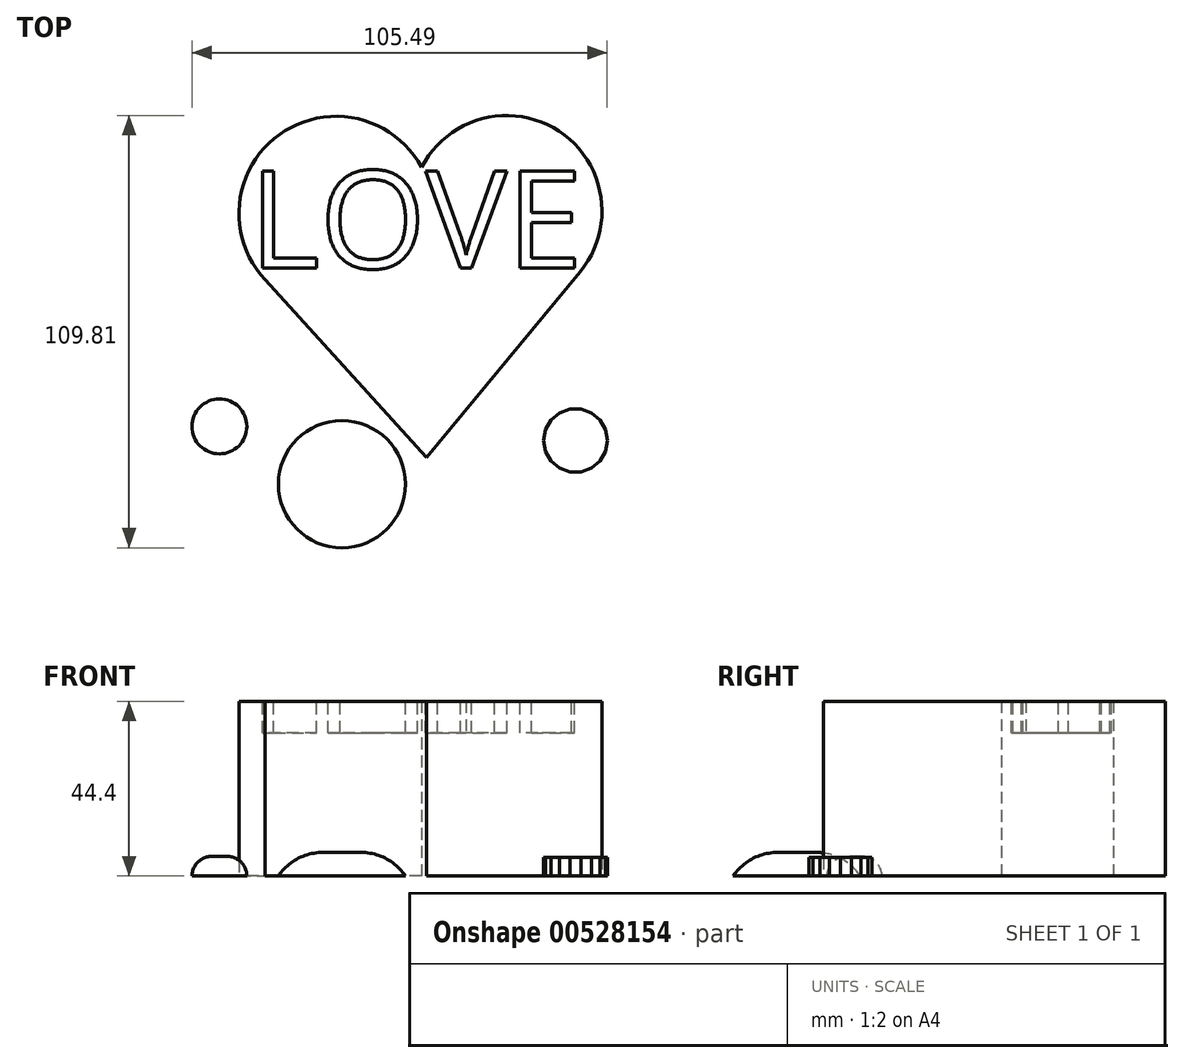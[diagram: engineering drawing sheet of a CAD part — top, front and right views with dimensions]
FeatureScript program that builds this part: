
annotation { "Feature Type Name" : "Feature", "Feature Type Description" : "" }
export const myFeature = defineFeature(function(context is Context, id is Id, definition is map)
    precondition{}
    {
        {
            var Q0;
            Q0=qCreatedBy(makeId("Top.planeOp"),FACE);
            var sketch = newSketch(context, id + "F0", { "sketchPlane" : qUnion([Q0])});
            skCircle(sketch, "E0", {"center": v(17.8, 25.02) * mm, "radius": 24.26 * mm});
            skCircle(sketch, "E1", {"center": v(-25.48, 24.4) * mm, "radius": 24.67 * mm});
            skLineSegment(sketch, "E2", {"start": v(-43.5, 7.56) * mm, "end": v(-2.46, -37.6) * mm});
            skLineSegment(sketch, "E3", {"start": v(-2.46, -37.6) * mm, "end": v(36.51, 9.57) * mm});
            skSolve(sketch);
        }
        {
            var Q0;
            {var subQ0=sQuery(id+"F0.wireOp",EDGE,"E1");var subQ1=sQuery(id+"F0.wireOp",EDGE,"E0");var subQ2=makeQuery(id+"F0.imprint","INTERSECT",VERTEX,{"disambiguationData":[OD(0.0)],"derivedFrom":[subQ1,subQ0]});Q0=makeQuery(id+"F0.imprint","IMPRINT",FACE,{"disambiguationData":[TD([[makeQuery(id+"F0.imprint","IMPRINT",EDGE,{"disambiguationData":[TD([[subQ2,-1.0]])],"derivedFrom":subQ1}),1.0]])]});}
            var Q1;
            {var subQ0=sQuery(id+"F0.wireOp",EDGE,"E0");var subQ1=makeQuery(id+"F0.imprint","INTERSECT",VERTEX,{"derivedFrom":[subQ0,sQuery(id+"F0.wireOp",EDGE,"E3")]});Q1=makeQuery(id+"F0.imprint","IMPRINT",FACE,{"disambiguationData":[TD([[makeQuery(id+"F0.imprint","IMPRINT",EDGE,{"disambiguationData":[TD([[subQ1,1.0]])],"derivedFrom":subQ0}),1.0]])]});}
            var Q2;
            {var subQ4=sQuery(id+"F0.wireOp",EDGE,"E2");Q2=makeQuery(id+"F0.imprint","IMPRINT",FACE,{"disambiguationData":[TD([[makeQuery(id+"F0.imprint","IMPRINT",EDGE,{"derivedFrom":subQ4}),1.0]])]});}
            var Q3;
            {var subQ0=sQuery(id+"F0.wireOp",EDGE,"E1");var subQ1=sQuery(id+"F0.wireOp",EDGE,"E0");var subQ2=makeQuery(id+"F0.imprint","INTERSECT",VERTEX,{"disambiguationData":[OD(0.0)],"derivedFrom":[subQ1,subQ0]});Q3=makeQuery(id+"F0.imprint","IMPRINT",FACE,{"disambiguationData":[TD([[makeQuery(id+"F0.imprint","IMPRINT",EDGE,{"disambiguationData":[TD([[subQ2,-1.0]])],"derivedFrom":subQ1}),-1.0]])]});}
            extrude(context, id + "F1", {"entities" : qUnion([Q0, Q1, Q2, Q3]), "depth" : 44.4 * mm, "offsetDistance" : 25 * mm});
        }
        {
            var Q0;
            Q0=makeQuery(id+"F1.opExtrude","CAP_FACE",FACE,{"disambiguationData":[OSD([sQuery(id+"F0.wireOp",EDGE,"E0"),sQuery(id+"F0.wireOp",EDGE,"E1"),sQuery(id+"F0.wireOp",EDGE,"E2"),sQuery(id+"F0.wireOp",EDGE,"E3")])],"isStart":false});
            var sketch = newSketch(context, id + "F2", { "sketchPlane" : qUnion([Q0])});
            skText(sketch, "E4", { "text": "LOVE", "fontName": "OpenSans-Regular.ttf"});
            const initialGuessF2  = {"E4": [-0.04758, 0.01047, 1, 0, 0.0249]};
            skSetInitialGuess(sketch, initialGuessF2);
            skSolve(sketch);
        }
        {
            var Q0;
            Q0 = qSketchRegion(id + "F2", true);
            extrude(context, id + "F3", {"entities" : qUnion([Q0]), "operationType" : NewBodyOperationType.REMOVE, "oppositeDirection" : true, "depth" : 8 * mm, "offsetDistance" : 25 * mm});
        }
        {
            var Q0;
            Q0=qCreatedBy(makeId("Top.planeOp"),FACE);
            var sketch = newSketch(context, id + "F4", { "sketchPlane" : qUnion([Q0])});
            skCircle(sketch, "E5", {"center": v(-55.11, -29.71) * mm, "radius": 6.97 * mm});
            skSolve(sketch);
        }
        {
            var Q0;
            Q0=makeQuery(id+"F4.imprint","IMPRINT",FACE,{"disambiguationData":[TD([[makeQuery(id+"F4.imprint","IMPRINT",EDGE,{"derivedFrom":sQuery(id+"F4.wireOp",EDGE,"E5")}),1.0]])]});
            extrude(context, id + "F5", {"entities" : qUnion([Q0]), "depth" : 5 * mm, "offsetDistance" : 25 * mm});
        }
        {
            var Q0;
            Q0=makeQuery(id+"F5.opExtrude","CAP_EDGE",EDGE,{"disambiguationData":[OSD([sQuery(id+"F4.wireOp",EDGE,"E5")])],"isStart":false});
            fillet(context, id + "F6", {"entities" : qUnion([Q0]), "radius" : 5.07 * mm, "tangentPropagation" : true, "allowEdgeOverflow" : false});
        }
        {
            var Q0;
            Q0=qCreatedBy(makeId("Top.planeOp"),FACE);
            var sketch = newSketch(context, id + "F7", { "sketchPlane" : qUnion([Q0])});
            skCircle(sketch, "E6.cCircle", {"center": v(35.3, -33.31) * mm, "radius": 7.98 * mm, "construction": true});
            skLineSegment(sketch, "E6.0", {"start": v(33.9, -25.33) * mm, "end": v(36.71, -25.33) * mm});
            skLineSegment(sketch, "E6.1", {"start": v(36.71, -25.33) * mm, "end": v(39.36, -26.3) * mm});
            skLineSegment(sketch, "E6.2", {"start": v(39.36, -26.3) * mm, "end": v(41.52, -28.1) * mm});
            skLineSegment(sketch, "E6.3", {"start": v(41.52, -28.1) * mm, "end": v(42.92, -30.54) * mm});
            skLineSegment(sketch, "E6.4", {"start": v(42.92, -30.54) * mm, "end": v(43.41, -33.31) * mm});
            skLineSegment(sketch, "E6.5", {"start": v(43.41, -33.31) * mm, "end": v(42.92, -36.08) * mm});
            skLineSegment(sketch, "E6.6", {"start": v(42.92, -36.08) * mm, "end": v(41.52, -38.52) * mm});
            skLineSegment(sketch, "E6.7", {"start": v(41.52, -38.52) * mm, "end": v(39.36, -40.33) * mm});
            skLineSegment(sketch, "E6.8", {"start": v(39.36, -40.33) * mm, "end": v(36.71, -41.3) * mm});
            skLineSegment(sketch, "E6.9", {"start": v(36.71, -41.3) * mm, "end": v(33.9, -41.3) * mm});
            skLineSegment(sketch, "E6.10", {"start": v(33.9, -41.3) * mm, "end": v(31.25, -40.33) * mm});
            skLineSegment(sketch, "E6.11", {"start": v(31.25, -40.33) * mm, "end": v(29.1, -38.52) * mm});
            skLineSegment(sketch, "E6.12", {"start": v(29.1, -38.52) * mm, "end": v(27.7, -36.08) * mm});
            skLineSegment(sketch, "E6.13", {"start": v(27.7, -36.08) * mm, "end": v(27.2, -33.31) * mm});
            skLineSegment(sketch, "E6.14", {"start": v(27.2, -33.31) * mm, "end": v(27.7, -30.54) * mm});
            skLineSegment(sketch, "E6.15", {"start": v(27.7, -30.54) * mm, "end": v(29.1, -28.1) * mm});
            skLineSegment(sketch, "E6.16", {"start": v(29.1, -28.1) * mm, "end": v(31.25, -26.3) * mm});
            skLineSegment(sketch, "E6.17", {"start": v(31.25, -26.3) * mm, "end": v(33.9, -25.33) * mm});
            skPoint(sketch, "E6.0.midPoint", {"position": v(35.3, -25.33) * mm});
            skSolve(sketch);
        }
        {
            var Q0;
            Q0=makeQuery(id+"F7.imprint","IMPRINT",FACE,{"disambiguationData":[TD([[makeQuery(id+"F7.imprint","IMPRINT",EDGE,{"derivedFrom":sQuery(id+"F7.wireOp",EDGE,"E6.0")}),-1.0]])]});
            extrude(context, id + "F8", {"entities" : qUnion([Q0]), "depth" : 4.7 * mm, "offsetDistance" : 25 * mm});
        }
        {
            var Q0;
            Q0=qCreatedBy(makeId("Top.planeOp"),FACE);
            var sketch = newSketch(context, id + "F9", { "sketchPlane" : qUnion([Q0])});
            skCircle(sketch, "E7", {"center": v(-24, -44.38) * mm, "radius": 16.15 * mm});
            skSolve(sketch);
        }
        {
            var Q0;
            Q0=makeQuery(id+"F9.imprint","IMPRINT",FACE,{"disambiguationData":[TD([[makeQuery(id+"F9.imprint","IMPRINT",EDGE,{"derivedFrom":sQuery(id+"F9.wireOp",EDGE,"E7")}),1.0]])]});
            extrude(context, id + "F10", {"entities" : qUnion([Q0]), "depth" : 6 * mm, "offsetDistance" : 25 * mm});
        }
        {
            var Q0;
            Q0=makeQuery(id+"F10.opExtrude","CAP_FACE",FACE,{"disambiguationData":[OSD([sQuery(id+"F9.wireOp",EDGE,"E7")])],"isStart":false});
            fillet(context, id + "F11", {"entities" : qUnion([Q0]), "radius" : 13.76 * mm, "tangentPropagation" : true, "allowEdgeOverflow" : false});
        }
    });
